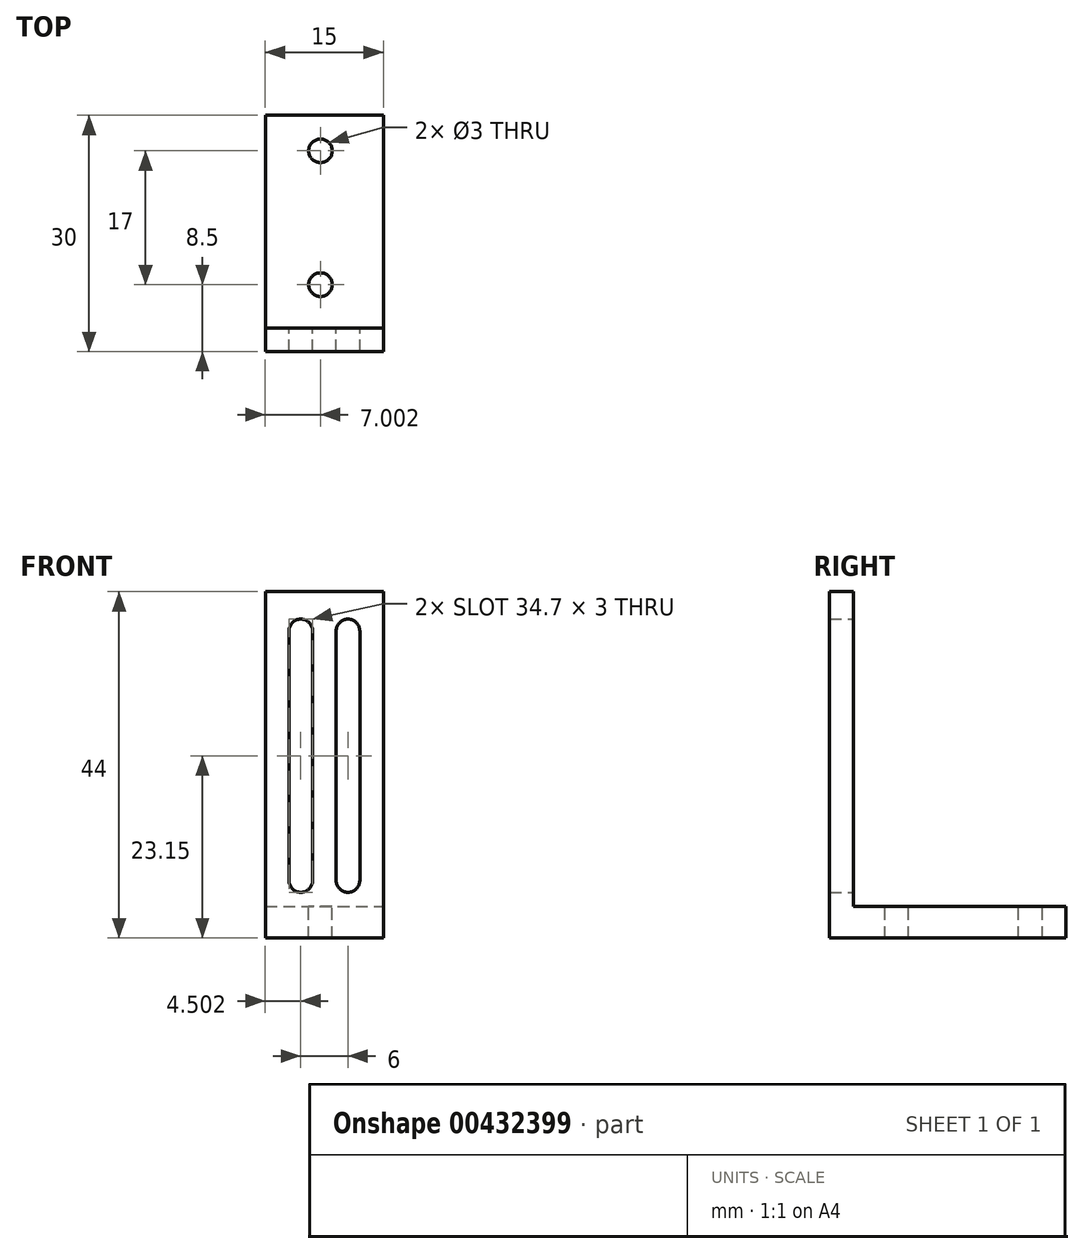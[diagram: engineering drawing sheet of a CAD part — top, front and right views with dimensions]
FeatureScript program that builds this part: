
annotation { "Feature Type Name" : "Feature", "Feature Type Description" : "" }
export const myFeature = defineFeature(function(context is Context, id is Id, definition is map)
    precondition{}
    {
        {
            var Q0;
            Q0=qCreatedBy(makeId("Top.planeOp"),FACE);
            var sketch = newSketch(context, id + "F0", { "sketchPlane" : qUnion([Q0])});
            skLineSegment(sketch, "E0.bottom", {"start": v(-1.34, 26.92) * mm, "end": v(13.66, 26.92) * mm});
            skLineSegment(sketch, "E0.top", {"start": v(-1.34, -3.08) * mm, "end": v(13.66, -3.08) * mm});
            skLineSegment(sketch, "E0.left", {"start": v(-1.34, 26.92) * mm, "end": v(-1.34, -3.08) * mm});
            skLineSegment(sketch, "E0.right", {"start": v(13.66, 26.92) * mm, "end": v(13.66, -3.08) * mm});
            skSolve(sketch);
        }
        {
            var Q0;
            Q0=makeQuery(id+"F0.imprint","IMPRINT",FACE,{"disambiguationData":[TD([[makeQuery(id+"F0.imprint","IMPRINT",EDGE,{"derivedFrom":sQuery(id+"F0.wireOp",EDGE,"E0.bottom")}),-1.0]])]});
            extrude(context, id + "F1", {"entities" : qUnion([Q0]), "depth" : 4 * mm});
        }
        {
            var Q0;
            Q0=makeQuery(id+"F1.opExtrude","CAP_FACE",FACE,{"disambiguationData":[OSD([sQuery(id+"F0.wireOp",EDGE,"E0.bottom"),sQuery(id+"F0.wireOp",EDGE,"E0.top"),sQuery(id+"F0.wireOp",EDGE,"E0.left"),sQuery(id+"F0.wireOp",EDGE,"E0.right")])],"isStart":false});
            var sketch = newSketch(context, id + "F2", { "sketchPlane" : qUnion([Q0])});
            skCircle(sketch, "E1", {"center": v(5.66, 5.42) * mm, "radius": 1.5 * mm});
            skCircle(sketch, "E2", {"center": v(5.66, 22.42) * mm, "radius": 1.5 * mm});
            skSolve(sketch);
        }
        {
            var Q0;
            Q0=makeQuery(id+"F2.imprint","IMPRINT",FACE,{"disambiguationData":[TD([[makeQuery(id+"F2.imprint","IMPRINT",EDGE,{"derivedFrom":sQuery(id+"F2.wireOp",EDGE,"E1")}),1.0]])]});
            var Q1;
            Q1=makeQuery(id+"F2.imprint","IMPRINT",FACE,{"disambiguationData":[TD([[makeQuery(id+"F2.imprint","IMPRINT",EDGE,{"derivedFrom":sQuery(id+"F2.wireOp",EDGE,"E2")}),1.0]])]});
            extrude(context, id + "F3", {"entities" : qUnion([Q0, Q1]), "operationType" : NewBodyOperationType.REMOVE, "oppositeDirection" : true, "depth" : 4 * mm});
        }
        {
            var Q0;
            Q0=makeQuery(id+"F1.opExtrude","CAP_FACE",FACE,{"disambiguationData":[OSD([sQuery(id+"F0.wireOp",EDGE,"E0.bottom"),sQuery(id+"F0.wireOp",EDGE,"E0.top"),sQuery(id+"F0.wireOp",EDGE,"E0.left"),sQuery(id+"F0.wireOp",EDGE,"E0.right")])],"isStart":false});
            var sketch = newSketch(context, id + "F4", { "sketchPlane" : qUnion([Q0])});
            skLineSegment(sketch, "E3.bottom", {"start": v(-1.34, -3.08) * mm, "end": v(13.66, -3.08) * mm});
            skLineSegment(sketch, "E3.top", {"start": v(-1.34, -0.08) * mm, "end": v(13.66, -0.08) * mm});
            skLineSegment(sketch, "E3.left", {"start": v(-1.34, -3.08) * mm, "end": v(-1.34, -0.08) * mm});
            skLineSegment(sketch, "E3.right", {"start": v(13.66, -3.08) * mm, "end": v(13.66, -0.08) * mm});
            skSolve(sketch);
        }
        {
            var Q0;
            Q0=makeQuery(id+"F4.imprint","IMPRINT",FACE,{"disambiguationData":[TD([[makeQuery(id+"F4.imprint","IMPRINT",EDGE,{"derivedFrom":sQuery(id+"F4.wireOp",EDGE,"E3.bottom")}),1.0]])]});
            extrude(context, id + "F5", {"entities" : qUnion([Q0]), "operationType" : NewBodyOperationType.ADD, "depth" : 40 * mm});
        }
        {
            var Q0;
            Q0=makeQuery(id+"F5.opExtrude","SWEPT_FACE",FACE,{"disambiguationData":[OSD([sQuery(id+"F4.wireOp",EDGE,"E3.top")])]});
            var sketch = newSketch(context, id + "F6", { "sketchPlane" : qUnion([Q0])});
            skCircle(sketch, "E4", {"center": v(-9.16, 39) * mm, "radius": 1.5 * mm});
            skCircle(sketch, "E5", {"center": v(-3.16, 39) * mm, "radius": 1.5 * mm});
            skLineSegment(sketch, "E6.bottom", {"start": v(-10.66, 39) * mm, "end": v(-7.66, 39) * mm});
            skLineSegment(sketch, "E6.top", {"start": v(-10.66, 7.3) * mm, "end": v(-7.66, 7.3) * mm});
            skLineSegment(sketch, "E6.left", {"start": v(-10.66, 39) * mm, "end": v(-10.66, 7.3) * mm});
            skLineSegment(sketch, "E6.right", {"start": v(-7.66, 39) * mm, "end": v(-7.66, 7.3) * mm});
            skLineSegment(sketch, "E7.bottom", {"start": v(-4.66, 39) * mm, "end": v(-1.66, 39) * mm});
            skLineSegment(sketch, "E7.top", {"start": v(-4.66, 7.3) * mm, "end": v(-1.66, 7.3) * mm});
            skLineSegment(sketch, "E7.left", {"start": v(-4.66, 39) * mm, "end": v(-4.66, 7.3) * mm});
            skLineSegment(sketch, "E7.right", {"start": v(-1.66, 39) * mm, "end": v(-1.66, 7.3) * mm});
            skCircle(sketch, "E8", {"center": v(-9.16, 7.3) * mm, "radius": 1.5 * mm});
            skCircle(sketch, "E9", {"center": v(-3.16, 7.3) * mm, "radius": 1.5 * mm});
            skSolve(sketch);
        }
        {
            var Q0;
            {var subQ0=sQuery(id+"F6.wireOp",EDGE,"E6.bottom");Q0=makeQuery(id+"F6.imprint","IMPRINT",FACE,{"disambiguationData":[TD([[makeQuery(id+"F6.imprint","IMPRINT",EDGE,{"derivedFrom":subQ0}),1.0]])]});}
            var Q1;
            {var subQ0=sQuery(id+"F6.wireOp",EDGE,"E6.bottom");Q1=makeQuery(id+"F6.imprint","IMPRINT",FACE,{"disambiguationData":[TD([[makeQuery(id+"F6.imprint","IMPRINT",EDGE,{"derivedFrom":subQ0}),-1.0]])]});}
            var Q2;
            {var subQ0=sQuery(id+"F6.wireOp",EDGE,"E6.left");Q2=makeQuery(id+"F6.imprint","IMPRINT",FACE,{"disambiguationData":[TD([[makeQuery(id+"F6.imprint","IMPRINT",EDGE,{"derivedFrom":subQ0}),1.0]])]});}
            var Q3;
            {var subQ0=sQuery(id+"F6.wireOp",EDGE,"E6.top");Q3=makeQuery(id+"F6.imprint","IMPRINT",FACE,{"disambiguationData":[TD([[makeQuery(id+"F6.imprint","IMPRINT",EDGE,{"derivedFrom":subQ0}),1.0]])]});}
            var Q4;
            {var subQ0=sQuery(id+"F6.wireOp",EDGE,"E7.top");Q4=makeQuery(id+"F6.imprint","IMPRINT",FACE,{"disambiguationData":[TD([[makeQuery(id+"F6.imprint","IMPRINT",EDGE,{"derivedFrom":subQ0}),-1.0]])]});}
            var Q5;
            {var subQ0=sQuery(id+"F6.wireOp",EDGE,"E7.top");Q5=makeQuery(id+"F6.imprint","IMPRINT",FACE,{"disambiguationData":[TD([[makeQuery(id+"F6.imprint","IMPRINT",EDGE,{"derivedFrom":subQ0}),1.0]])]});}
            var Q6;
            {var subQ0=sQuery(id+"F6.wireOp",EDGE,"E6.top");Q6=makeQuery(id+"F6.imprint","IMPRINT",FACE,{"disambiguationData":[TD([[makeQuery(id+"F6.imprint","IMPRINT",EDGE,{"derivedFrom":subQ0}),-1.0]])]});}
            var Q7;
            {var subQ0=sQuery(id+"F6.wireOp",EDGE,"E7.left");Q7=makeQuery(id+"F6.imprint","IMPRINT",FACE,{"disambiguationData":[TD([[makeQuery(id+"F6.imprint","IMPRINT",EDGE,{"derivedFrom":subQ0}),1.0]])]});}
            var Q8;
            {var subQ0=sQuery(id+"F6.wireOp",EDGE,"E7.bottom");Q8=makeQuery(id+"F6.imprint","IMPRINT",FACE,{"disambiguationData":[TD([[makeQuery(id+"F6.imprint","IMPRINT",EDGE,{"derivedFrom":subQ0}),-1.0]])]});}
            var Q9;
            {var subQ0=sQuery(id+"F6.wireOp",EDGE,"E7.bottom");Q9=makeQuery(id+"F6.imprint","IMPRINT",FACE,{"disambiguationData":[TD([[makeQuery(id+"F6.imprint","IMPRINT",EDGE,{"derivedFrom":subQ0}),1.0]])]});}
            extrude(context, id + "F7", {"entities" : qUnion([Q0, Q1, Q2, Q3, Q4, Q5, Q6, Q7, Q8, Q9]), "operationType" : NewBodyOperationType.REMOVE, "oppositeDirection" : true, "depth" : 5.33 * mm});
        }
    });
